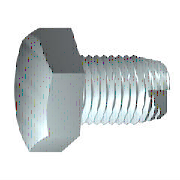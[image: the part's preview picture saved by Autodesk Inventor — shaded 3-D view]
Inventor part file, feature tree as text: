
AUTODESK INVENTOR PART (.ipt)
format: ipt  version: 2015 (Build 190159000, 159)  size: 190,464 bytes
history: native  units: mm (DEFAULTED — no unit token found)
features: sketch x2, extrude x1, chamfer x1, plane x1
ambient origin geometry x8: Origin, YZ Plane, XZ Plane, XY Plane, X Axis, Y Axis, Z Axis, Center Point
bodies: Solid1 (feature_tree), Body (feature_tree)
feature tree (5):
  extrude  "Head"  TaperAngle=90.0deg  [1 undecoded]
  chamfer  "Chamfer1"  [1 undecoded]
  plane  "Work Plane1"
  sketch  "Sketch1"  dims[d0=7.9375mm d12=90.0deg]
  sketch  "Sketch2"  dims[d1=5.842mm d2=0.0mm d21=90.0deg d3=0.0mm d4=12.7mm d5=38.1mm d6=0.0mm d7=38.1mm d8=12.7mm d9=0.70485mm d10=4.9276mm d11=30.0deg d13=0.0mm d109=45.0deg d110=0.0mm]
note: 2 required parameter values undecoded (feature->parameter linkage not recoverable at this tier; creation-order binding heuristic only, values carry confidence <= 0.55)
